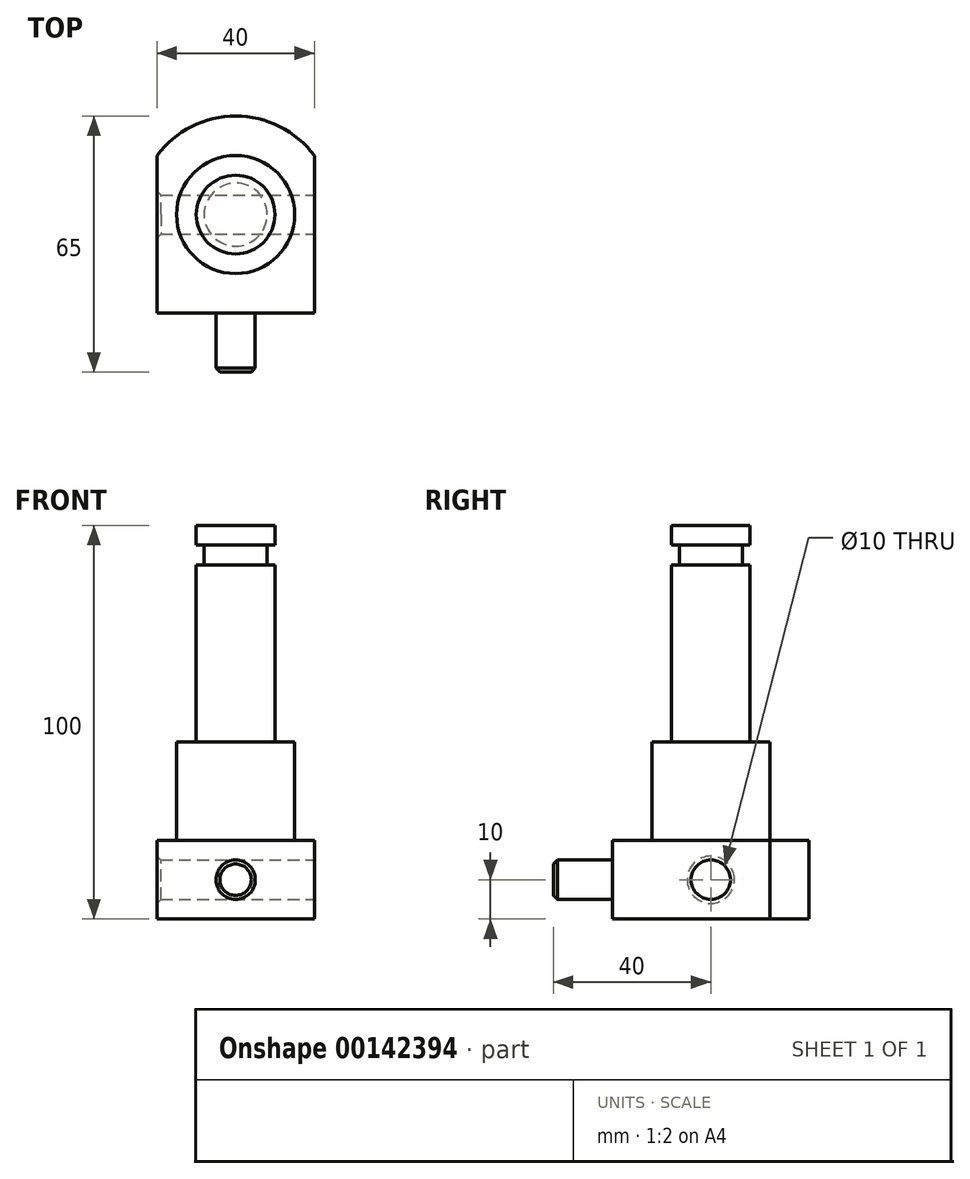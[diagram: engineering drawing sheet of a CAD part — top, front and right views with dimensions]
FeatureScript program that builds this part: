
annotation { "Feature Type Name" : "Feature", "Feature Type Description" : "" }
export const myFeature = defineFeature(function(context is Context, id is Id, definition is map)
    precondition{}
    {
        {
            var Q0;
            Q0=qCreatedBy(makeId("Top.planeOp"),FACE);
            var sketch = newSketch(context, id + "F0", { "sketchPlane" : qUnion([Q0])});
            skLineSegment(sketch, "E0.bottom", {"start": v(0, 0) * mm, "end": v(-40, 0) * mm});
            skLineSegment(sketch, "E0.left", {"start": v(0, 0) * mm, "end": v(0, 40) * mm});
            skLineSegment(sketch, "E0.right", {"start": v(-40, 0) * mm, "end": v(-40, 40) * mm});
            skArc(sketch, "E1", {"start": v(0, 40) * mm, "mid": v(-20, 50) * mm, "end": v(-40, 40) * mm});
            skSolve(sketch);
        }
        {
            var Q0;
            Q0=makeQuery(id+"F0.imprint","IMPRINT",FACE,{"disambiguationData":[TD([[makeQuery(id+"F0.imprint","IMPRINT",EDGE,{"derivedFrom":sQuery(id+"F0.wireOp",EDGE,"E0.bottom")}),-1.0]])]});
            extrude(context, id + "F1", {"entities" : qUnion([Q0]), "depth" : 20 * mm});
        }
        {
            var Q0;
            Q0=makeQuery(id+"F1.opExtrude","SWEPT_FACE",FACE,{"disambiguationData":[OSD([sQuery(id+"F0.wireOp",EDGE,"E0.bottom")])]});
            var sketch = newSketch(context, id + "F2", { "sketchPlane" : qUnion([Q0])});
            skLineSegment(sketch, "E2", {"start": v(-20, 0) * mm, "end": v(-20, 20) * mm, "construction": true});
            skLineSegment(sketch, "E3", {"start": v(-40, 10) * mm, "end": v(0, 10) * mm, "construction": true});
            skCircle(sketch, "E4", {"center": v(-20, 10) * mm, "radius": 5 * mm});
            skSolve(sketch);
        }
        {
            var Q0;
            Q0=makeQuery(id+"F2.imprint","IMPRINT",FACE,{"disambiguationData":[TD([[makeQuery(id+"F2.imprint","IMPRINT",EDGE,{"derivedFrom":sQuery(id+"F2.wireOp",EDGE,"E4")}),1.0]])]});
            extrude(context, id + "F3", {"entities" : qUnion([Q0]), "operationType" : NewBodyOperationType.ADD, "depth" : 15 * mm});
        }
        {
            var Q0;
            Q0=makeQuery(id+"F1.opExtrude","CAP_FACE",FACE,{"disambiguationData":[OSD([sQuery(id+"F0.wireOp",EDGE,"E0.bottom"),sQuery(id+"F0.wireOp",EDGE,"E0.left"),sQuery(id+"F0.wireOp",EDGE,"E0.right"),sQuery(id+"F0.wireOp",EDGE,"E1")])],"isStart":false});
            var sketch = newSketch(context, id + "F4", { "sketchPlane" : qUnion([Q0])});
            skCircle(sketch, "E5", {"center": v(-20, 25) * mm, "radius": 15 * mm});
            skSolve(sketch);
        }
        {
            var Q0;
            Q0=makeQuery(id+"F4.imprint","IMPRINT",FACE,{"disambiguationData":[TD([[makeQuery(id+"F4.imprint","IMPRINT",EDGE,{"derivedFrom":sQuery(id+"F4.wireOp",EDGE,"E5")}),1.0]])]});
            extrude(context, id + "F5", {"entities" : qUnion([Q0]), "operationType" : NewBodyOperationType.ADD, "depth" : 25 * mm});
        }
        {
            var Q0;
            Q0=makeQuery(id+"F5.opExtrude","CAP_FACE",FACE,{"disambiguationData":[OSD([sQuery(id+"F4.wireOp",EDGE,"E5")])],"isStart":false});
            var sketch = newSketch(context, id + "F6", { "sketchPlane" : qUnion([Q0])});
            skCircle(sketch, "E6", {"center": v(-20, 25) * mm, "radius": 10 * mm});
            skSolve(sketch);
        }
        {
            var Q0;
            Q0=makeQuery(id+"F6.imprint","IMPRINT",FACE,{"disambiguationData":[TD([[makeQuery(id+"F6.imprint","IMPRINT",EDGE,{"derivedFrom":sQuery(id+"F6.wireOp",EDGE,"E6")}),1.0]])]});
            extrude(context, id + "F7", {"entities" : qUnion([Q0]), "operationType" : NewBodyOperationType.ADD, "depth" : 45 * mm});
        }
        {
            var Q0;
            Q0=makeQuery(id+"F7.opExtrude","CAP_FACE",FACE,{"disambiguationData":[OSD([sQuery(id+"F6.wireOp",EDGE,"E6")])],"isStart":false});
            var sketch = newSketch(context, id + "F8", { "sketchPlane" : qUnion([Q0])});
            skCircle(sketch, "E7", {"center": v(-20, 25) * mm, "radius": 8 * mm});
            skSolve(sketch);
        }
        {
            var Q0;
            Q0=makeQuery(id+"F8.imprint","IMPRINT",FACE,{"disambiguationData":[TD([[makeQuery(id+"F8.imprint","IMPRINT",EDGE,{"derivedFrom":sQuery(id+"F8.wireOp",EDGE,"E7")}),1.0]])]});
            extrude(context, id + "F9", {"entities" : qUnion([Q0]), "operationType" : NewBodyOperationType.ADD, "depth" : 5 * mm});
        }
        {
            var Q0;
            Q0=makeQuery(id+"F9.opExtrude","CAP_FACE",FACE,{"disambiguationData":[OSD([sQuery(id+"F8.wireOp",EDGE,"E7")])],"isStart":false});
            var sketch = newSketch(context, id + "F10", { "sketchPlane" : qUnion([Q0])});
            skCircle(sketch, "E8", {"center": v(-20, 25) * mm, "radius": 10 * mm});
            skSolve(sketch);
        }
        {
            var Q0;
            Q0=makeQuery(id+"F10.imprint","IMPRINT",FACE,{"disambiguationData":[TD([[makeQuery(id+"F10.imprint","IMPRINT",EDGE,{"derivedFrom":sQuery(id+"F10.wireOp",EDGE,"E8")}),1.0]])]});
            var Q1;
            Q1=makeQuery(id+"F10.imprint","IMPRINT",FACE,{"disambiguationData":[TD([[makeQuery(id+"F10.imprint","IMPRINT",EDGE,{"derivedFrom":makeQuery(id+"F9.opExtrude","CAP_EDGE",EDGE,{"disambiguationData":[OSD([sQuery(id+"F8.wireOp",EDGE,"E7")])],"isStart":false})}),1.0]])]});
            extrude(context, id + "F11", {"entities" : qUnion([Q0, Q1]), "operationType" : NewBodyOperationType.ADD, "depth" : 5 * mm});
        }
        {
            var Q0;
            Q0=makeQuery(id+"F1.opExtrude","SWEPT_FACE",FACE,{"disambiguationData":[OSD([sQuery(id+"F0.wireOp",EDGE,"E0.left")])]});
            var sketch = newSketch(context, id + "F12", { "sketchPlane" : qUnion([Q0])});
            skLineSegment(sketch, "E9", {"start": v(20, 20) * mm, "end": v(20, 0) * mm, "construction": true});
            skLineSegment(sketch, "E10", {"start": v(0, 10) * mm, "end": v(40, 10) * mm, "construction": true});
            skCircle(sketch, "E11", {"center": v(25, 10) * mm, "radius": 5 * mm});
            skSolve(sketch);
        }
        {
            var Q0;
            Q0=makeQuery(id+"F12.imprint","IMPRINT",FACE,{"disambiguationData":[TD([[makeQuery(id+"F12.imprint","IMPRINT",EDGE,{"derivedFrom":sQuery(id+"F12.wireOp",EDGE,"E11")}),1.0]])]});
            extrude(context, id + "F13", {"entities" : qUnion([Q0]), "operationType" : NewBodyOperationType.REMOVE, "oppositeDirection" : true, "depth" : 45 * mm});
        }
        {
            var Q0;
            Q0=makeQuery(id+"F3.opExtrude","CAP_EDGE",EDGE,{"disambiguationData":[OSD([sQuery(id+"F2.wireOp",EDGE,"E4")])],"isStart":false});
            var Q1;
            Q1=makeQuery(id+"F13.boolean.opBoolean","COPY",EDGE,{"derivedFrom":makeQuery(id+"F13.opExtrude","CAP_EDGE",EDGE,{"disambiguationData":[OSD([sQuery(id+"F12.wireOp",EDGE,"E11")])],"isStart":true})});
            var Q2;
            Q2=makeQuery(id+"F13.boolean.opBoolean","INTERSECT",EDGE,{"derivedFrom":[makeQuery(id+"F1.opExtrude","SWEPT_FACE",FACE,{"disambiguationData":[OSD([sQuery(id+"F0.wireOp",EDGE,"E0.right")])]}),makeQuery(id+"F13.opExtrude","SWEPT_FACE",FACE,{"disambiguationData":[OSD([sQuery(id+"F12.wireOp",EDGE,"E11")])]})]});
            chamfer(context, id + "F14", {"entities" : qUnion([Q0, Q1, Q2]), "width" : 1 * mm, "tangentPropagation" : true});
        }
    });
